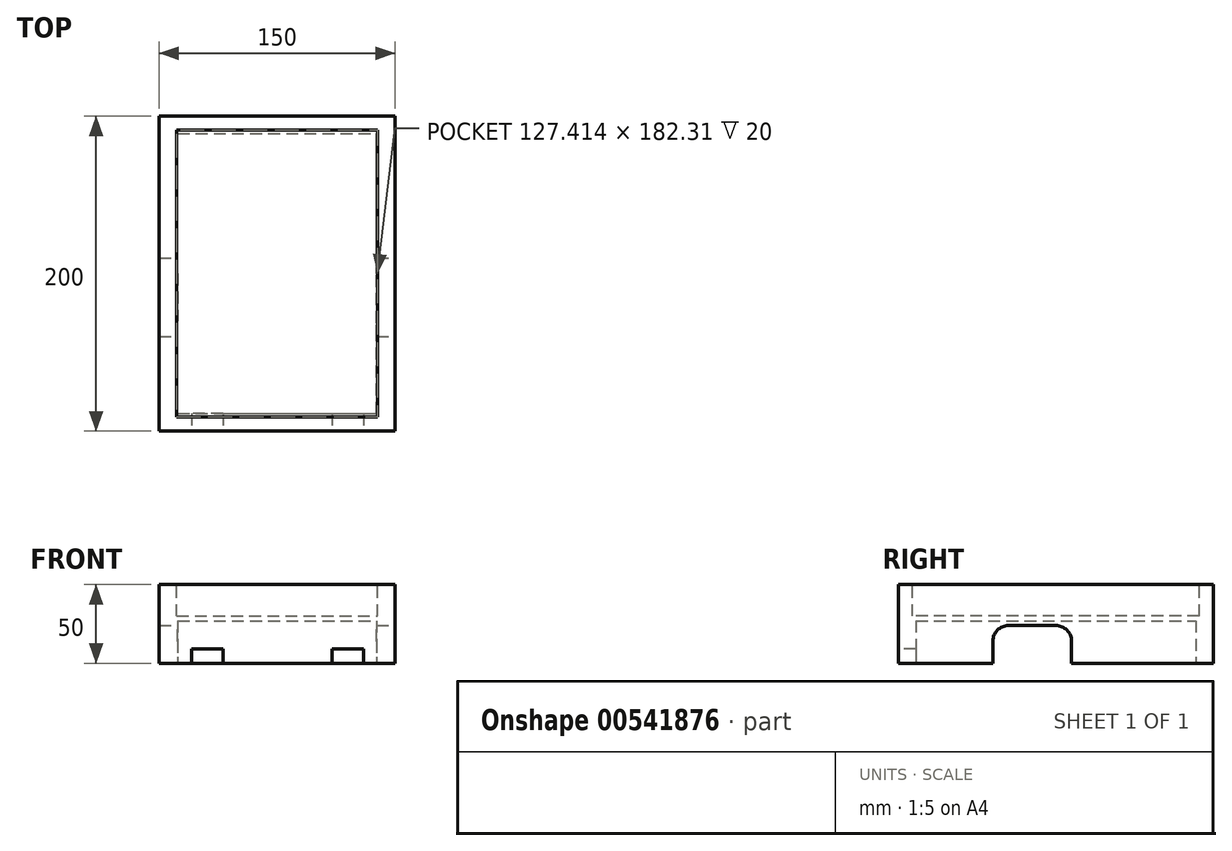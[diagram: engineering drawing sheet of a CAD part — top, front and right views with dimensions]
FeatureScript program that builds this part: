
annotation { "Feature Type Name" : "Feature", "Feature Type Description" : "" }
export const myFeature = defineFeature(function(context is Context, id is Id, definition is map)
    precondition{}
    {
        {
            var Q0;
            Q0=qCreatedBy(makeId("Right.planeOp"),FACE);
            var sketch = newSketch(context, id + "F0", { "sketchPlane" : qUnion([Q0])});
            skLineSegment(sketch, "E0.bottom", {"start": v(0, 0) * mm, "end": v(200, 0) * mm});
            skLineSegment(sketch, "E0.top", {"start": v(0, 50) * mm, "end": v(200, 50) * mm});
            skLineSegment(sketch, "E0.left", {"start": v(0, 0) * mm, "end": v(0, 50) * mm});
            skLineSegment(sketch, "E0.right", {"start": v(200, 0) * mm, "end": v(200, 50) * mm});
            skSolve(sketch);
        }
        {
            var Q0;
            Q0=makeQuery(id+"F0.imprint","IMPRINT",FACE,{"disambiguationData":[TD([[makeQuery(id+"F0.imprint","IMPRINT",EDGE,{"derivedFrom":sQuery(id+"F0.wireOp",EDGE,"E0.bottom")}),1.0]])]});
            extrude(context, id + "F1", {"entities" : qUnion([Q0]), "endBound" : BoundingType.SYMMETRIC, "depth" : 150 * mm, "offsetDistance" : 25 * mm});
        }
        {
            var Q0;
            Q0=makeQuery(id+"F1.opExtrude","SWEPT_FACE",FACE,{"disambiguationData":[OSD([sQuery(id+"F0.wireOp",EDGE,"E0.top")])]});
            var sketch = newSketch(context, id + "F2", { "sketchPlane" : qUnion([Q0])});
            skLineSegment(sketch, "E1.bottom", {"start": v(-63.7, 191.16) * mm, "end": v(63.7, 191.16) * mm});
            skLineSegment(sketch, "E1.top", {"start": v(-63.7, 8.84) * mm, "end": v(63.7, 8.84) * mm});
            skLineSegment(sketch, "E1.left", {"start": v(-63.7, 191.16) * mm, "end": v(-63.7, 8.84) * mm});
            skLineSegment(sketch, "E1.right", {"start": v(63.7, 191.16) * mm, "end": v(63.7, 8.84) * mm});
            skPoint(sketch, "E1.middle", {"position": v(0, 100) * mm});
            skPoint(sketch, "E1.middle.positionSnap0", {"position": v(-75, 100) * mm});
            skPoint(sketch, "E1.centerSnap0", {"position": v(-75, 100) * mm});
            skSolve(sketch);
        }
        {
            var Q0;
            Q0=makeQuery(id+"F2.imprint","IMPRINT",FACE,{"disambiguationData":[TD([[makeQuery(id+"F2.imprint","IMPRINT",EDGE,{"derivedFrom":sQuery(id+"F2.wireOp",EDGE,"E1.bottom")}),-1.0]])]});
            extrude(context, id + "F3", {"entities" : qUnion([Q0]), "operationType" : NewBodyOperationType.REMOVE, "oppositeDirection" : true, "depth" : 20 * mm, "offsetDistance" : 25 * mm});
        }
        {
            var Q0;
            Q0=makeQuery(id+"F1.opExtrude","SWEPT_FACE",FACE,{"disambiguationData":[OSD([sQuery(id+"F0.wireOp",EDGE,"E0.left")])]});
            var sketch = newSketch(context, id + "F4", { "sketchPlane" : qUnion([Q0])});
            skLineSegment(sketch, "E2", {"start": v(-74.46, 0) * mm, "end": v(-54.46, 0) * mm});
            skLineSegment(sketch, "E3", {"start": v(75, 0) * mm, "end": v(55, 0) * mm});
            skLineSegment(sketch, "E4.bottom", {"start": v(-54.46, 0) * mm, "end": v(-34.46, 0) * mm});
            skLineSegment(sketch, "E4.top", {"start": v(-54.46, 9) * mm, "end": v(-34.46, 9) * mm});
            skLineSegment(sketch, "E4.left", {"start": v(-54.46, 0) * mm, "end": v(-54.46, 9) * mm});
            skLineSegment(sketch, "E4.right", {"start": v(-34.46, 0) * mm, "end": v(-34.46, 9) * mm});
            skLineSegment(sketch, "E5.bottom", {"start": v(55, 0) * mm, "end": v(35, 0) * mm});
            skLineSegment(sketch, "E5.top", {"start": v(55, 9) * mm, "end": v(35, 9) * mm});
            skLineSegment(sketch, "E5.left", {"start": v(55, 0) * mm, "end": v(55, 9) * mm});
            skLineSegment(sketch, "E5.right", {"start": v(35, 0) * mm, "end": v(35, 9) * mm});
            skSolve(sketch);
        }
        {
            var Q0;
            Q0=makeQuery(id+"F1.opExtrude","SWEPT_FACE",FACE,{"disambiguationData":[OSD([sQuery(id+"F0.wireOp",EDGE,"E0.bottom")])]});
            var sketch = newSketch(context, id + "F5", { "sketchPlane" : qUnion([Q0])});
            skLineSegment(sketch, "E6.bottom", {"start": v(-63.15, -11.12) * mm, "end": v(63.15, -11.12) * mm});
            skLineSegment(sketch, "E6.top", {"start": v(-63.15, -188.88) * mm, "end": v(63.15, -188.88) * mm});
            skLineSegment(sketch, "E6.left", {"start": v(-63.15, -11.12) * mm, "end": v(-63.15, -188.88) * mm});
            skLineSegment(sketch, "E6.right", {"start": v(63.15, -11.12) * mm, "end": v(63.15, -188.88) * mm});
            skPoint(sketch, "E6.middle", {"position": v(0, -100) * mm});
            skPoint(sketch, "E6.middle.positionSnap0", {"position": v(-75, -100) * mm});
            skPoint(sketch, "E6.centerSnap0", {"position": v(-75, -100) * mm});
            skSolve(sketch);
        }
        {
            var Q0;
            Q0=makeQuery(id+"F5.imprint","IMPRINT",FACE,{"disambiguationData":[TD([[makeQuery(id+"F5.imprint","IMPRINT",EDGE,{"derivedFrom":sQuery(id+"F5.wireOp",EDGE,"E6.bottom")}),-1.0]])]});
            extrude(context, id + "F6", {"entities" : qUnion([Q0]), "operationType" : NewBodyOperationType.REMOVE, "oppositeDirection" : true, "depth" : 27 * mm, "offsetDistance" : 25 * mm});
        }
        {
            var Q0;
            Q0=makeQuery(id+"F4.imprint","IMPRINT",FACE,{"disambiguationData":[TD([[makeQuery(id+"F4.imprint","IMPRINT",EDGE,{"derivedFrom":sQuery(id+"F4.wireOp",EDGE,"E5.bottom")}),-1.0]])]});
            var Q1;
            Q1=makeQuery(id+"F4.imprint","IMPRINT",FACE,{"disambiguationData":[TD([[makeQuery(id+"F4.imprint","IMPRINT",EDGE,{"derivedFrom":sQuery(id+"F4.wireOp",EDGE,"E4.bottom")}),-1.0]])]});
            extrude(context, id + "F7", {"entities" : qUnion([Q0, Q1]), "operationType" : NewBodyOperationType.REMOVE, "oppositeDirection" : true, "depth" : 25 * mm, "offsetDistance" : 25 * mm});
        }
        {
            var Q0;
            Q0=makeQuery(id+"F1.opExtrude","CAP_FACE",FACE,{"disambiguationData":[OSD([sQuery(id+"F0.wireOp",EDGE,"E0.bottom"),sQuery(id+"F0.wireOp",EDGE,"E0.top"),sQuery(id+"F0.wireOp",EDGE,"E0.left"),sQuery(id+"F0.wireOp",EDGE,"E0.right")])],"isStart":false});
            var sketch = newSketch(context, id + "F8", { "sketchPlane" : qUnion([Q0])});
            skLineSegment(sketch, "E7", {"start": v(60, 0) * mm, "end": v(60, 14) * mm});
            skLineSegment(sketch, "E8", {"start": v(70, 24) * mm, "end": v(100, 24) * mm});
            skLineSegment(sketch, "E9", {"start": v(110, 14) * mm, "end": v(110, 0) * mm});
            skPoint(sketch, "E10.visualSharp", {"position": v(60, 24) * mm});
            skArc(sketch, "E10.filletArc", {"start": v(70, 24) * mm, "mid": v(62.93, 21.07) * mm, "end": v(60, 14) * mm});
            skPoint(sketch, "E11.visualSharp", {"position": v(110, 24) * mm});
            skArc(sketch, "E11.filletArc", {"start": v(110, 14) * mm, "mid": v(107.07, 21.07) * mm, "end": v(100, 24) * mm});
            skSolve(sketch);
        }
        {
            var Q0;
            {var subQ1=sQuery(id+"F8.wireOp",EDGE,"E7");Q0=makeQuery(id+"F8.imprint","IMPRINT",FACE,{"disambiguationData":[TD([[makeQuery(id+"F8.imprint","IMPRINT",EDGE,{"derivedFrom":subQ1}),-1.0]])]});}
            extrude(context, id + "F9", {"entities" : qUnion([Q0]), "operationType" : NewBodyOperationType.REMOVE, "oppositeDirection" : true, "depth" : 160 * mm, "offsetDistance" : 25 * mm});
        }
    });
